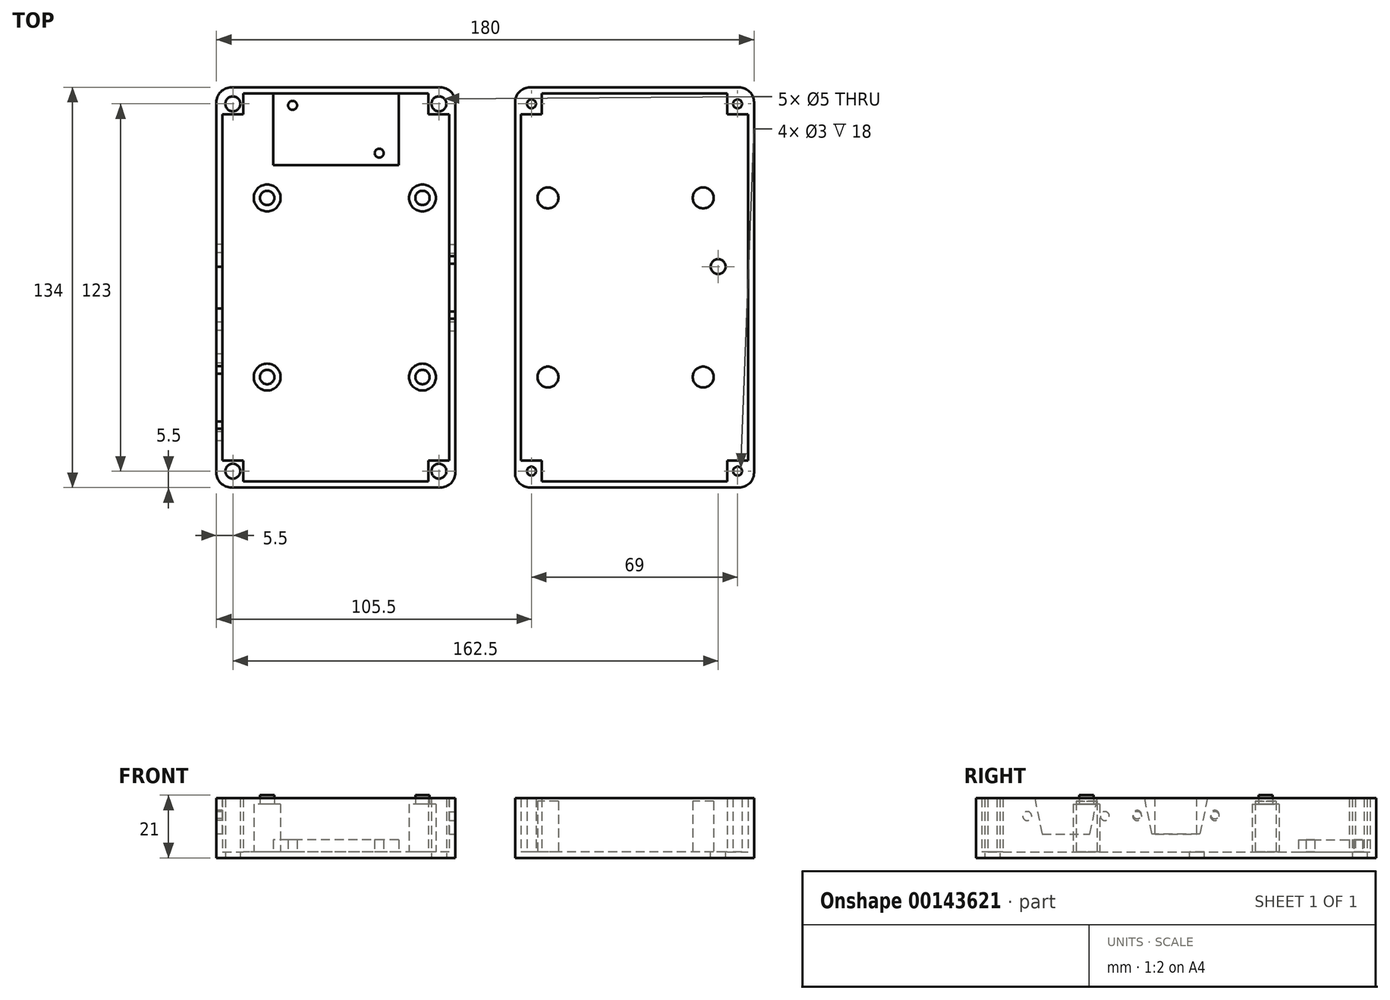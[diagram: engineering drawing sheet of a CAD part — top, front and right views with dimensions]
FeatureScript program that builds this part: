
annotation { "Feature Type Name" : "Feature", "Feature Type Description" : "" }
export const myFeature = defineFeature(function(context is Context, id is Id, definition is map)
    precondition{}
    {
        {
            var Q0;
            Q0=qCreatedBy(makeId("Top.planeOp"),FACE);
            var sketch = newSketch(context, id + "F0", { "sketchPlane" : qUnion([Q0])});
            skLineSegment(sketch, "E0.bottom", {"start": v(35, -67) * mm, "end": v(-35, -67) * mm});
            skLineSegment(sketch, "E0.top", {"start": v(35, 67) * mm, "end": v(-35, 67) * mm});
            skLineSegment(sketch, "E0.left", {"start": v(40, -62) * mm, "end": v(40, 62) * mm});
            skLineSegment(sketch, "E0.right", {"start": v(-40, -62) * mm, "end": v(-40, 62) * mm});
            skPoint(sketch, "E0.middle", {"position": v(0, 0) * mm});
            skPoint(sketch, "E1.visualSharp", {"position": v(40, 67) * mm});
            skArc(sketch, "E1.filletArc", {"start": v(40, 62) * mm, "mid": v(38.54, 65.54) * mm, "end": v(35, 67) * mm});
            skPoint(sketch, "E2.visualSharp", {"position": v(40, -67) * mm});
            skArc(sketch, "E2.filletArc", {"start": v(35, -67) * mm, "mid": v(38.54, -65.54) * mm, "end": v(40, -62) * mm});
            skPoint(sketch, "E3.visualSharp", {"position": v(-40, 67) * mm});
            skArc(sketch, "E3.filletArc", {"start": v(-35, 67) * mm, "mid": v(-38.54, 65.54) * mm, "end": v(-40, 62) * mm});
            skPoint(sketch, "E4.visualSharp", {"position": v(-40, -67) * mm});
            skArc(sketch, "E4.filletArc", {"start": v(-40, -62) * mm, "mid": v(-38.54, -65.54) * mm, "end": v(-35, -67) * mm});
            skSolve(sketch);
        }
        {
            var Q0;
            Q0=qSketchRegion(id+"F0",true);
            extrude(context, id + "F1", {"entities" : qUnion([Q0]), "depth" : 20 * mm});
        }
        {
            var Q0;
            Q0=makeQuery(id+"F1.opExtrude","CAP_FACE",FACE,{"disambiguationData":[OSD([sQuery(id+"F0.wireOp",EDGE,"E0.bottom"),sQuery(id+"F0.wireOp",EDGE,"E0.top"),sQuery(id+"F0.wireOp",EDGE,"E0.left"),sQuery(id+"F0.wireOp",EDGE,"E0.right")])],"isStart":false});
            shell(context, id + "F2", {"entities" : qUnion([Q0]), "thickness" : 2 * mm});
        }
        {
            var Q0;
            Q0=makeQuery(id+"F2.opShell","OFFSET_FACE",FACE,{"disambiguationData":[OSD([sQuery(id+"F0.wireOp",EDGE,"E0.bottom"),sQuery(id+"F0.wireOp",EDGE,"E0.top"),sQuery(id+"F0.wireOp",EDGE,"E0.left"),sQuery(id+"F0.wireOp",EDGE,"E0.right")])]});
            var sketch = newSketch(context, id + "F3", { "sketchPlane" : qUnion([Q0])});
            skCircle(sketch, "E5", {"center": v(29, 30) * mm, "radius": 4.5 * mm});
            skCircle(sketch, "E6", {"center": v(-23, 30) * mm, "radius": 4.5 * mm});
            skCircle(sketch, "E7", {"center": v(29, -30) * mm, "radius": 4.5 * mm});
            skCircle(sketch, "E8", {"center": v(-23, -30) * mm, "radius": 4.5 * mm});
            skLineSegment(sketch, "E9.bottom", {"start": v(29, -21) * mm, "end": v(5, -21) * mm, "construction": true});
            skLineSegment(sketch, "E9.top", {"start": v(29, 21) * mm, "end": v(5, 21) * mm, "construction": true});
            skLineSegment(sketch, "E9.left", {"start": v(29, -21) * mm, "end": v(29, 21) * mm, "construction": true});
            skLineSegment(sketch, "E9.right", {"start": v(5, -21) * mm, "end": v(5, 21) * mm, "construction": true});
            skPoint(sketch, "E9.middle", {"position": v(17, 0) * mm});
            skCircle(sketch, "E10", {"center": v(9, -14.5) * mm, "radius": 1.4 * mm, "construction": true});
            skCircle(sketch, "E11", {"center": v(25, 14.5) * mm, "radius": 1.4 * mm, "construction": true});
            skLineSegment(sketch, "E12.bottom", {"start": v(21, 41) * mm, "end": v(-21, 41) * mm});
            skLineSegment(sketch, "E12.top", {"start": v(21, 65) * mm, "end": v(-21, 65) * mm});
            skLineSegment(sketch, "E12.left", {"start": v(21, 41) * mm, "end": v(21, 65) * mm});
            skLineSegment(sketch, "E12.right", {"start": v(-21, 41) * mm, "end": v(-21, 65) * mm});
            skPoint(sketch, "E12.middle", {"position": v(0, 53) * mm});
            skCircle(sketch, "E13", {"center": v(-14.5, 61) * mm, "radius": 1.5 * mm});
            skCircle(sketch, "E14", {"center": v(14.5, 45) * mm, "radius": 1.5 * mm});
            skCircle(sketch, "E15", {"center": v(34.5, -61.5) * mm, "radius": 2.5 * mm});
            skLineSegment(sketch, "E16.bottom", {"start": v(38, -65) * mm, "end": v(31, -65) * mm});
            skLineSegment(sketch, "E16.top", {"start": v(38, -58) * mm, "end": v(31, -58) * mm});
            skLineSegment(sketch, "E16.left", {"start": v(38, -65) * mm, "end": v(38, -58) * mm});
            skLineSegment(sketch, "E16.right", {"start": v(31, -65) * mm, "end": v(31, -58) * mm});
            skLineSegment(sketch, "E17.bottom", {"start": v(38, 58) * mm, "end": v(31, 58) * mm});
            skLineSegment(sketch, "E17.top", {"start": v(38, 65) * mm, "end": v(31, 65) * mm});
            skLineSegment(sketch, "E17.left", {"start": v(38, 58) * mm, "end": v(38, 65) * mm});
            skLineSegment(sketch, "E17.right", {"start": v(31, 58) * mm, "end": v(31, 65) * mm});
            skPoint(sketch, "E17.middle", {"position": v(34.5, 61.5) * mm});
            skCircle(sketch, "E18", {"center": v(34.5, 61.5) * mm, "radius": 2.5 * mm});
            skLineSegment(sketch, "E19.MirrorCS", {"start": v(-31, -65) * mm, "end": v(-31, -58) * mm});
            skLineSegment(sketch, "E20.MirrorCS", {"start": v(-38, -65) * mm, "end": v(-31, -65) * mm});
            skCircle(sketch, "E21.MirrorC", {"center": v(-34.5, -61.5) * mm, "radius": 2.5 * mm});
            skLineSegment(sketch, "E22.MirrorCS", {"start": v(-38, -58) * mm, "end": v(-31, -58) * mm});
            skLineSegment(sketch, "E23.MirrorCS", {"start": v(-38, -65) * mm, "end": v(-38, -58) * mm});
            skLineSegment(sketch, "E24.MirrorCS", {"start": v(-31, 58) * mm, "end": v(-31, 65) * mm});
            skCircle(sketch, "E25.MirrorC", {"center": v(-34.5, 61.5) * mm, "radius": 2.5 * mm});
            skLineSegment(sketch, "E26.MirrorCS", {"start": v(-38, 58) * mm, "end": v(-38, 65) * mm});
            skLineSegment(sketch, "E27.MirrorCS", {"start": v(-38, 65) * mm, "end": v(-31, 65) * mm});
            skLineSegment(sketch, "E28.MirrorCS", {"start": v(-38, 58) * mm, "end": v(-31, 58) * mm});
            skSolve(sketch);
        }
        {
            var Q0;
            Q0=makeQuery(id+"F3.imprint","IMPRINT",FACE,{"disambiguationData":[TD([[makeQuery(id+"F3.imprint","IMPRINT",EDGE,{"derivedFrom":sQuery(id+"F3.wireOp",EDGE,"E6")}),1.0]])]});
            var Q1;
            Q1=makeQuery(id+"F3.imprint","IMPRINT",FACE,{"disambiguationData":[TD([[makeQuery(id+"F3.imprint","IMPRINT",EDGE,{"derivedFrom":sQuery(id+"F3.wireOp",EDGE,"E5")}),1.0]])]});
            var Q2;
            Q2=makeQuery(id+"F3.imprint","IMPRINT",FACE,{"disambiguationData":[TD([[makeQuery(id+"F3.imprint","IMPRINT",EDGE,{"derivedFrom":sQuery(id+"F3.wireOp",EDGE,"E7")}),1.0]])]});
            var Q3;
            Q3=makeQuery(id+"F3.imprint","IMPRINT",FACE,{"disambiguationData":[TD([[makeQuery(id+"F3.imprint","IMPRINT",EDGE,{"derivedFrom":sQuery(id+"F3.wireOp",EDGE,"E8")}),1.0]])]});
            extrude(context, id + "F4", {"entities" : qUnion([Q0, Q1, Q2, Q3]), "operationType" : NewBodyOperationType.ADD, "depth" : 16 * mm});
        }
        {
            var Q0;
            Q0=makeQuery(id+"F4.opExtrude","CAP_FACE",FACE,{"disambiguationData":[OSD([sQuery(id+"F3.wireOp",EDGE,"E6")])],"isStart":false});
            var Q1;
            Q1=makeQuery(id+"F4.opExtrude","CAP_FACE",FACE,{"disambiguationData":[OSD([sQuery(id+"F3.wireOp",EDGE,"E5")])],"isStart":false});
            cPlane(context, id + "F5", {"entities" : qUnion([Q0, Q1]), "cplaneType" : CPlaneType.MID_PLANE, "offset" : 17 * mm, "width" : 150 * mm, "height" : 150 * mm});
        }
        {
            var Q0;
            Q0=qCreatedBy(id+"F5.planeOp",FACE);
            var sketch = newSketch(context, id + "F6", { "sketchPlane" : qUnion([Q0])});
            skCircle(sketch, "E29", {"center": v(-23, 30) * mm, "radius": 2.4 * mm});
            skCircle(sketch, "E30", {"center": v(29, 30) * mm, "radius": 2.4 * mm});
            skCircle(sketch, "E31", {"center": v(29, -30) * mm, "radius": 2.4 * mm});
            skCircle(sketch, "E32", {"center": v(-23, -30) * mm, "radius": 2.4 * mm});
            skSolve(sketch);
        }
        {
            var Q0;
            Q0=qSketchRegion(id+"F6",true);
            extrude(context, id + "F7", {"entities" : qUnion([Q0]), "operationType" : NewBodyOperationType.ADD, "depth" : 3 * mm});
        }
        {
            var Q0;
            Q0=makeQuery(id+"F3.imprint","IMPRINT",FACE,{"disambiguationData":[TD([[makeQuery(id+"F3.imprint","IMPRINT",EDGE,{"derivedFrom":sQuery(id+"F3.wireOp",EDGE,"E12.bottom")}),-1.0]])]});
            extrude(context, id + "F8", {"entities" : qUnion([Q0]), "operationType" : NewBodyOperationType.ADD, "depth" : 4 * mm});
        }
        {
            var Q0;
            Q0=makeQuery(id+"F1.opExtrude","SWEPT_FACE",FACE,{"disambiguationData":[OSD([sQuery(id+"F0.wireOp",EDGE,"E0.right")])]});
            var sketch = newSketch(context, id + "F9", { "sketchPlane" : qUnion([Q0])});
            skCircle(sketch, "E33", {"center": v(-13, 14.5) * mm, "radius": 1.4 * mm});
            skCircle(sketch, "E34", {"center": v(13, 14.5) * mm, "radius": 1.4 * mm});
            skLineSegment(sketch, "E35.bottom", {"start": v(7, 8) * mm, "end": v(-7, 8) * mm});
            skLineSegment(sketch, "E35.top", {"start": v(7, 20) * mm, "end": v(-7, 20) * mm});
            skLineSegment(sketch, "E35.left", {"start": v(7, 8) * mm, "end": v(7, 20) * mm});
            skLineSegment(sketch, "E35.right", {"start": v(-7, 8) * mm, "end": v(-7, 20) * mm});
            skPoint(sketch, "E35.middle", {"position": v(0, 14) * mm});
            skCircle(sketch, "E36", {"center": v(23.83, 14) * mm, "radius": 1.5 * mm});
            skCircle(sketch, "E37", {"center": v(49.83, 14) * mm, "radius": 1.5 * mm});
            skLineSegment(sketch, "E38", {"start": v(26.33, 20) * mm, "end": v(47.33, 20) * mm});
            skLineSegment(sketch, "E39", {"start": v(47.33, 20) * mm, "end": v(44.83, 8) * mm});
            skLineSegment(sketch, "E40", {"start": v(44.83, 8) * mm, "end": v(28.83, 8) * mm});
            skLineSegment(sketch, "E41", {"start": v(28.83, 8) * mm, "end": v(26.33, 20) * mm});
            skSolve(sketch);
        }
        {
            var Q0;
            Q0=qSketchRegion(id+"F9",true);
            extrude(context, id + "F10", {"entities" : qUnion([Q0]), "operationType" : NewBodyOperationType.REMOVE, "oppositeDirection" : true, "depth" : 2 * mm});
        }
        {
            var Q0;
            Q0=makeQuery(id+"F1.opExtrude","SWEPT_FACE",FACE,{"disambiguationData":[OSD([sQuery(id+"F0.wireOp",EDGE,"E0.left")])]});
            var sketch = newSketch(context, id + "F11", { "sketchPlane" : qUnion([Q0])});
            skCircle(sketch, "E42", {"center": v(-13, 14) * mm, "radius": 1.5 * mm});
            skCircle(sketch, "E43", {"center": v(13, 14) * mm, "radius": 1.5 * mm});
            skLineSegment(sketch, "E44", {"start": v(-10.5, 20) * mm, "end": v(10.5, 20) * mm});
            skLineSegment(sketch, "E45", {"start": v(10.5, 20) * mm, "end": v(8, 8) * mm});
            skLineSegment(sketch, "E46", {"start": v(8, 8) * mm, "end": v(-8, 8) * mm});
            skLineSegment(sketch, "E47", {"start": v(-8, 8) * mm, "end": v(-10.5, 20) * mm});
            skSolve(sketch);
        }
        {
            var Q0;
            Q0=qSketchRegion(id+"F11",true);
            extrude(context, id + "F12", {"entities" : qUnion([Q0]), "operationType" : NewBodyOperationType.REMOVE, "oppositeDirection" : true, "depth" : 2 * mm});
        }
        {
            var Q0;
            {var subQ4=sQuery(id+"F3.wireOp",EDGE,"E17.bottom");Q0=makeQuery(id+"F3.imprint","IMPRINT",FACE,{"disambiguationData":[TD([[makeQuery(id+"F3.imprint","IMPRINT",EDGE,{"derivedFrom":subQ4}),-1.0]])]});}
            var Q1;
            Q1=makeQuery(id+"F3.imprint","IMPRINT",FACE,{"disambiguationData":[TD([[makeQuery(id+"F3.imprint","IMPRINT",EDGE,{"derivedFrom":sQuery(id+"F3.wireOp",EDGE,"E15")}),-1.0]])]});
            var Q2;
            {var subQ3=sQuery(id+"F3.wireOp",EDGE,"E24.MirrorCS");Q2=makeQuery(id+"F3.imprint","IMPRINT",FACE,{"disambiguationData":[TD([[makeQuery(id+"F3.imprint","IMPRINT",EDGE,{"derivedFrom":subQ3}),1.0]])]});}
            var Q3;
            {var subQ1=sQuery(id+"F3.wireOp",EDGE,"E19.MirrorCS");Q3=makeQuery(id+"F3.imprint","IMPRINT",FACE,{"disambiguationData":[TD([[makeQuery(id+"F3.imprint","IMPRINT",EDGE,{"derivedFrom":subQ1}),1.0]])]});}
            extrude(context, id + "F13", {"entities" : qUnion([Q0, Q1, Q2, Q3]), "operationType" : NewBodyOperationType.ADD, "depth" : 18 * mm});
        }
        {
            var Q0;
            Q0=qCreatedBy(makeId("Top.planeOp"),FACE);
            var sketch = newSketch(context, id + "F14", { "sketchPlane" : qUnion([Q0])});
            skLineSegment(sketch, "E48.bottom", {"start": v(135, -67) * mm, "end": v(65, -67) * mm});
            skLineSegment(sketch, "E48.top", {"start": v(135, 67) * mm, "end": v(65, 67) * mm});
            skLineSegment(sketch, "E48.left", {"start": v(140, -62) * mm, "end": v(140, 62) * mm});
            skLineSegment(sketch, "E48.right", {"start": v(60, -62) * mm, "end": v(60, 62) * mm});
            skPoint(sketch, "E48.middle", {"position": v(100, 0) * mm});
            skPoint(sketch, "E49.visualSharp", {"position": v(60, 67) * mm});
            skArc(sketch, "E49.filletArc", {"start": v(65, 67) * mm, "mid": v(61.46, 65.54) * mm, "end": v(60, 62) * mm});
            skPoint(sketch, "E50.visualSharp", {"position": v(140, 67) * mm});
            skArc(sketch, "E50.filletArc", {"start": v(140, 62) * mm, "mid": v(138.54, 65.54) * mm, "end": v(135, 67) * mm});
            skPoint(sketch, "E51.visualSharp", {"position": v(60, -67) * mm});
            skArc(sketch, "E51.filletArc", {"start": v(60, -62) * mm, "mid": v(61.46, -65.54) * mm, "end": v(65, -67) * mm});
            skPoint(sketch, "E52.visualSharp", {"position": v(140, -67) * mm});
            skArc(sketch, "E52.filletArc", {"start": v(135, -67) * mm, "mid": v(138.54, -65.54) * mm, "end": v(140, -62) * mm});
            skSolve(sketch);
        }
        {
            var Q0;
            Q0=qSketchRegion(id+"F14",true);
            extrude(context, id + "F15", {"entities" : qUnion([Q0]), "depth" : 20 * mm});
        }
        {
            var Q0;
            Q0=qCreatedBy(makeId("Right.planeOp"),FACE);
            cPlane(context, id + "F16", {"entities" : qUnion([Q0]), "cplaneType" : CPlaneType.OFFSET, "offset" : 100 * mm, "width" : 150 * mm, "height" : 150 * mm});
        }
        {
            var Q0;
            Q0=makeQuery(id+"F15.opExtrude","CAP_FACE",FACE,{"disambiguationData":[OSD([sQuery(id+"F14.wireOp",EDGE,"E48.bottom"),sQuery(id+"F14.wireOp",EDGE,"E48.top"),sQuery(id+"F14.wireOp",EDGE,"E48.left"),sQuery(id+"F14.wireOp",EDGE,"E48.right"),sQuery(id+"F14.wireOp",EDGE,"E49.filletArc"),sQuery(id+"F14.wireOp",EDGE,"E50.filletArc"),sQuery(id+"F14.wireOp",EDGE,"E51.filletArc"),sQuery(id+"F14.wireOp",EDGE,"E52.filletArc")])],"isStart":false});
            shell(context, id + "F17", {"entities" : qUnion([Q0]), "thickness" : 2 * mm});
        }
        {
            var Q0;
            Q0=makeQuery(id+"F17.opShell","OFFSET_FACE",FACE,{"disambiguationData":[OSD([sQuery(id+"F14.wireOp",EDGE,"E48.bottom"),sQuery(id+"F14.wireOp",EDGE,"E48.top"),sQuery(id+"F14.wireOp",EDGE,"E48.left"),sQuery(id+"F14.wireOp",EDGE,"E48.right"),sQuery(id+"F14.wireOp",EDGE,"E49.filletArc"),sQuery(id+"F14.wireOp",EDGE,"E50.filletArc"),sQuery(id+"F14.wireOp",EDGE,"E51.filletArc"),sQuery(id+"F14.wireOp",EDGE,"E52.filletArc")])]});
            var sketch = newSketch(context, id + "F18", { "sketchPlane" : qUnion([Q0])});
            skLineSegment(sketch, "E53.bottom", {"start": v(69, 58) * mm, "end": v(62, 58) * mm});
            skLineSegment(sketch, "E53.top", {"start": v(69, 65) * mm, "end": v(62, 65) * mm});
            skLineSegment(sketch, "E53.left", {"start": v(69, 58) * mm, "end": v(69, 65) * mm});
            skLineSegment(sketch, "E53.right", {"start": v(62, 58) * mm, "end": v(62, 65) * mm});
            skPoint(sketch, "E53.middle", {"position": v(65.5, 61.5) * mm});
            skCircle(sketch, "E54", {"center": v(65.5, 61.5) * mm, "radius": 1.5 * mm});
            skCircle(sketch, "E55", {"center": v(71, 30) * mm, "radius": 3.5 * mm});
            skCircle(sketch, "E56", {"center": v(123, 30) * mm, "radius": 3.5 * mm});
            skCircle(sketch, "E57", {"center": v(123, -30) * mm, "radius": 3.5 * mm});
            skCircle(sketch, "E58", {"center": v(71, -30) * mm, "radius": 3.5 * mm});
            skLineSegment(sketch, "E59.bottom", {"start": v(69, -58) * mm, "end": v(62, -58) * mm});
            skLineSegment(sketch, "E59.top", {"start": v(69, -65) * mm, "end": v(62, -65) * mm});
            skLineSegment(sketch, "E59.left", {"start": v(69, -58) * mm, "end": v(69, -65) * mm});
            skLineSegment(sketch, "E59.right", {"start": v(62, -58) * mm, "end": v(62, -65) * mm});
            skPoint(sketch, "E59.middle", {"position": v(65.5, -61.5) * mm});
            skCircle(sketch, "E60", {"center": v(65.5, -61.5) * mm, "radius": 1.5 * mm});
            skLineSegment(sketch, "E61.MirrorCS", {"start": v(131, -65) * mm, "end": v(138, -65) * mm});
            skLineSegment(sketch, "E62.MirrorCS", {"start": v(138, -58) * mm, "end": v(138, -65) * mm});
            skLineSegment(sketch, "E63.MirrorCS", {"start": v(131, -58) * mm, "end": v(131, -65) * mm});
            skCircle(sketch, "E64.MirrorC", {"center": v(134.5, -61.5) * mm, "radius": 1.5 * mm});
            skLineSegment(sketch, "E65.MirrorCS", {"start": v(131, -58) * mm, "end": v(138, -58) * mm});
            skLineSegment(sketch, "E66.MirrorCS", {"start": v(138, 58) * mm, "end": v(138, 65) * mm});
            skLineSegment(sketch, "E67.MirrorCS", {"start": v(131, 65) * mm, "end": v(138, 65) * mm});
            skLineSegment(sketch, "E68.MirrorCS", {"start": v(131, 58) * mm, "end": v(138, 58) * mm});
            skLineSegment(sketch, "E69.MirrorCS", {"start": v(131, 58) * mm, "end": v(131, 65) * mm});
            skCircle(sketch, "E70.MirrorC", {"center": v(134.5, 61.5) * mm, "radius": 1.5 * mm});
            skCircle(sketch, "E71", {"center": v(128, 7) * mm, "radius": 2.5 * mm});
            skSolve(sketch);
        }
        {
            var Q0;
            Q0=makeQuery(id+"F18.imprint","IMPRINT",FACE,{"disambiguationData":[TD([[makeQuery(id+"F18.imprint","IMPRINT",EDGE,{"derivedFrom":sQuery(id+"F18.wireOp",EDGE,"E56")}),1.0]])]});
            var Q1;
            Q1=makeQuery(id+"F18.imprint","IMPRINT",FACE,{"disambiguationData":[TD([[makeQuery(id+"F18.imprint","IMPRINT",EDGE,{"derivedFrom":sQuery(id+"F18.wireOp",EDGE,"E57")}),1.0]])]});
            var Q2;
            Q2=makeQuery(id+"F18.imprint","IMPRINT",FACE,{"disambiguationData":[TD([[makeQuery(id+"F18.imprint","IMPRINT",EDGE,{"derivedFrom":sQuery(id+"F18.wireOp",EDGE,"E58")}),1.0]])]});
            var Q3;
            Q3=makeQuery(id+"F18.imprint","IMPRINT",FACE,{"disambiguationData":[TD([[makeQuery(id+"F18.imprint","IMPRINT",EDGE,{"derivedFrom":sQuery(id+"F18.wireOp",EDGE,"E55")}),1.0]])]});
            extrude(context, id + "F19", {"entities" : qUnion([Q0, Q1, Q2, Q3]), "operationType" : NewBodyOperationType.ADD, "depth" : 17 * mm});
        }
        {
            var Q0;
            {var subQ6=sQuery(id+"F18.wireOp",EDGE,"E53.bottom");Q0=makeQuery(id+"F18.imprint","IMPRINT",FACE,{"disambiguationData":[TD([[makeQuery(id+"F18.imprint","IMPRINT",EDGE,{"derivedFrom":subQ6}),-1.0]])]});}
            var Q1;
            {var subQ5=sQuery(id+"F18.wireOp",EDGE,"E68.MirrorCS");Q1=makeQuery(id+"F18.imprint","IMPRINT",FACE,{"disambiguationData":[TD([[makeQuery(id+"F18.imprint","IMPRINT",EDGE,{"derivedFrom":subQ5}),1.0]])]});}
            var Q2;
            {var subQ6=sQuery(id+"F18.wireOp",EDGE,"E59.bottom");Q2=makeQuery(id+"F18.imprint","IMPRINT",FACE,{"disambiguationData":[TD([[makeQuery(id+"F18.imprint","IMPRINT",EDGE,{"derivedFrom":subQ6}),1.0]])]});}
            var Q3;
            {var subQ5=sQuery(id+"F18.wireOp",EDGE,"E63.MirrorCS");Q3=makeQuery(id+"F18.imprint","IMPRINT",FACE,{"disambiguationData":[TD([[makeQuery(id+"F18.imprint","IMPRINT",EDGE,{"derivedFrom":subQ5}),1.0]])]});}
            extrude(context, id + "F20", {"entities" : qUnion([Q0, Q1, Q2, Q3]), "operationType" : NewBodyOperationType.ADD, "depth" : 18 * mm});
        }
        {
            var Q0;
            Q0=sQuery(id+"F3.wireOp",VERTEX,"E25.MirrorC.center");
            var Q1;
            Q1=sQuery(id+"F3.wireOp",VERTEX,"E17.middle");
            var Q2;
            Q2=sQuery(id+"F3.wireOp",VERTEX,"E21.MirrorC.center");
            var Q3;
            Q3=sQuery(id+"F3.wireOp",VERTEX,"E15.center");
            var Q4;
            Q4=makeQuery(id+"F1.opExtrude","SWEPT_BODY",BODY,{"disambiguationData":[OSD([sQuery(id+"F0.wireOp",EDGE,"E0.bottom"),sQuery(id+"F0.wireOp",EDGE,"E0.top"),sQuery(id+"F0.wireOp",EDGE,"E0.left"),sQuery(id+"F0.wireOp",EDGE,"E0.right"),sQuery(id+"F0.wireOp",EDGE,"E1.filletArc"),sQuery(id+"F0.wireOp",EDGE,"E2.filletArc"),sQuery(id+"F0.wireOp",EDGE,"E3.filletArc"),sQuery(id+"F0.wireOp",EDGE,"E4.filletArc")])]});
            hole(context, id + "F21", {"style" : HoleStyle.SIMPLE, "endStyle" : HoleEndStyle.THROUGH, "holeDiameter" : 5 * mm, "locations" : qUnion([Q0, Q1, Q2, Q3]), "scope" : qUnion([Q4]), "isTappedThrough" : true});
        }
        {
            var Q0;
            Q0=sQuery(id+"F18.wireOp",VERTEX,"E71.center");
            var Q1;
            Q1=makeQuery(id+"F15.opExtrude","SWEPT_BODY",BODY,{"disambiguationData":[OSD([sQuery(id+"F14.wireOp",EDGE,"E48.bottom"),sQuery(id+"F14.wireOp",EDGE,"E48.top"),sQuery(id+"F14.wireOp",EDGE,"E48.left"),sQuery(id+"F14.wireOp",EDGE,"E48.right"),sQuery(id+"F14.wireOp",EDGE,"E49.filletArc"),sQuery(id+"F14.wireOp",EDGE,"E50.filletArc"),sQuery(id+"F14.wireOp",EDGE,"E51.filletArc"),sQuery(id+"F14.wireOp",EDGE,"E52.filletArc")])]});
            hole(context, id + "F22", {"style" : HoleStyle.SIMPLE, "endStyle" : HoleEndStyle.THROUGH, "holeDiameter" : 5 * mm, "locations" : qUnion([Q0]), "scope" : qUnion([Q1]), "isTappedThrough" : true});
        }
    });
